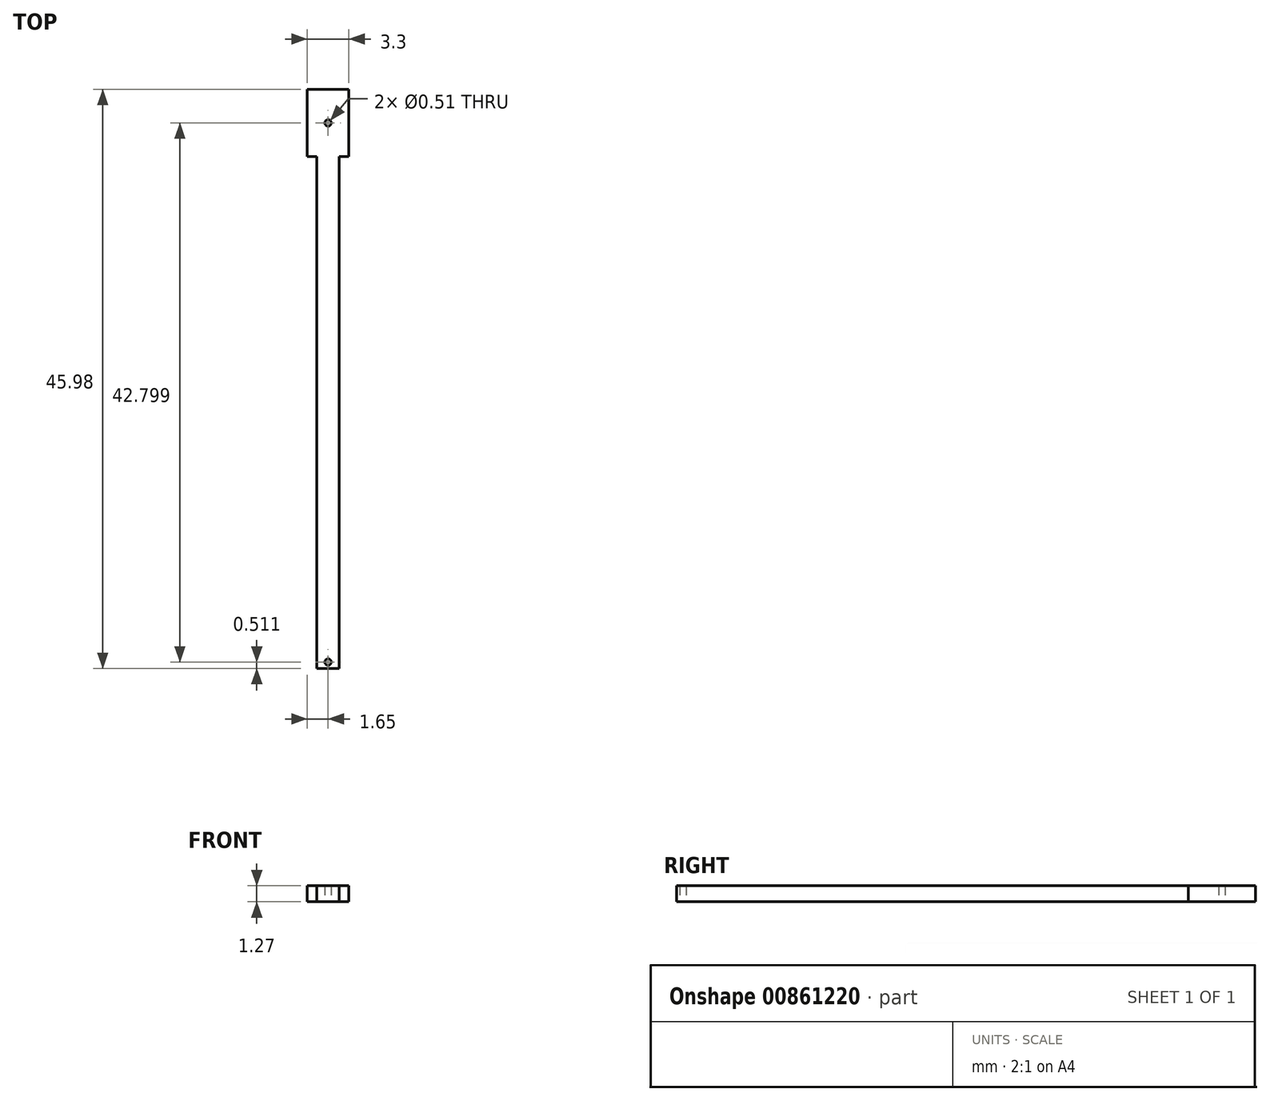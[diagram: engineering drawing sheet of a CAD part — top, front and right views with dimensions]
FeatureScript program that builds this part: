
annotation { "Feature Type Name" : "Feature", "Feature Type Description" : "" }
export const myFeature = defineFeature(function(context is Context, id is Id, definition is map)
    precondition{}
    {
        {
            var Q0;
            Q0=qCreatedBy(makeId("Top.planeOp"),FACE);
            var sketch = newSketch(context, id + "F0", { "sketchPlane" : qUnion([Q0])});
            skLineSegment(sketch, "E0.bottom", {"start": v(1.65, -2.67) * mm, "end": v(0.89, -2.67) * mm});
            skLineSegment(sketch, "E0.top", {"start": v(1.65, 2.67) * mm, "end": v(-1.65, 2.67) * mm});
            skLineSegment(sketch, "E0.left", {"start": v(1.65, -2.67) * mm, "end": v(1.65, 2.67) * mm});
            skLineSegment(sketch, "E0.right", {"start": v(-1.65, -2.67) * mm, "end": v(-1.65, 2.67) * mm});
            skPoint(sketch, "E0.middle", {"position": v(0, 0) * mm});
            skLineSegment(sketch, "E1", {"start": v(-0.89, -2.67) * mm, "end": v(-0.89, -43.3) * mm});
            skLineSegment(sketch, "E2", {"start": v(-0.89, -43.3) * mm, "end": v(0.89, -43.3) * mm});
            skLineSegment(sketch, "E3", {"start": v(0.89, -2.67) * mm, "end": v(0.89, -43.3) * mm});
            skLineSegment(sketch, "E4.trimOffspring", {"start": v(-0.89, -2.67) * mm, "end": v(-1.65, -2.67) * mm});
            skCircle(sketch, "E5", {"center": v(0, -42.8) * mm, "radius": 0.25 * mm});
            skCircle(sketch, "E6", {"center": v(0, 0) * mm, "radius": 0.25 * mm});
            skSolve(sketch);
        }
        {
            var Q0;
            Q0 = qSketchRegion(id + "F0", true);
            extrude(context, id + "F1", {"entities" : qUnion([Q0]), "depth" : 1.27 * mm, "offsetDistance" : 25.4 * mm});
        }
    });
